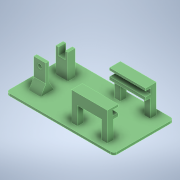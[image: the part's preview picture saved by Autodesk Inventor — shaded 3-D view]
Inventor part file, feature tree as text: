
AUTODESK INVENTOR PART (.ipt)
format: ipt  version: 2022 (Build 260153000, 153)  size: 257,024 bytes
history: native  units: mm
features: extrude x10, sketch x10
ambient origin geometry x8: Origin, YZ Plane, XZ Plane, XY Plane, X Axis, Y Axis, Z Axis, Center Point
bodies: 实体1 (feature_tree)
feature tree (20):
  extrude  "拉伸1"  Depth=100.0mm
  extrude  "拉伸2"  Depth=4.0mm TaperAngle=0.0deg
  extrude  "拉伸3"  Depth=10.0mm
  extrude  "拉伸4"  Depth=40.0mm
  extrude  "拉伸5"  Depth=30.0mm TaperAngle=0.0deg
  extrude  "拉伸6"  Depth=18.0mm
  extrude  "拉伸7"  Depth=9.0mm TaperAngle=0.0deg
  extrude  "拉伸8"  Depth=17.0mm
  extrude  "拉伸9"  Depth=12.0mm
  extrude  "拉伸11"  Depth=29.0mm TaperAngle=0.0deg
  sketch  "草图1"  dims[d0=180.0mm d1=100.0mm]
  sketch  "草图2"  dims[d2=5.0mm d3=4.0mm d4=0.0mm]
  sketch  "草图3"  dims[d5=61.8mm d6=10.0mm]
  sketch  "草图4"  dims[d7=10.0mm d8=40.0mm]
  sketch  "草图5"  dims[d9=20.0mm d10=30.0mm d11=0.0mm]
  sketch  "草图6"  dims[d12=5.0mm d13=0.0mm d14=18.0mm]
  sketch  "草图7"  dims[d15=18.0mm d16=9.0mm d17=0.0mm]
  sketch  "草图8"  dims[d18=4.0mm d19=0.0mm d20=17.0mm]
  sketch  "草图9"  dims[d21=20.0mm d22=12.0mm]
  sketch  "草图10"  dims[d23=22.0mm d24=29.0mm d25=0.0mm d26=4.5mm d27=4.5mm d28=13.0mm d29=0.0mm d30=37.0mm d31=5.0mm d32=20.0mm d33=45.0mm d34=0.0mm d35=7.2mm d36=35.099mm d37=10.0mm d38=0.0mm d39=9.0mm d40=9.0mm d41=15.0mm d44=20.0mm d45=0.0mm]
